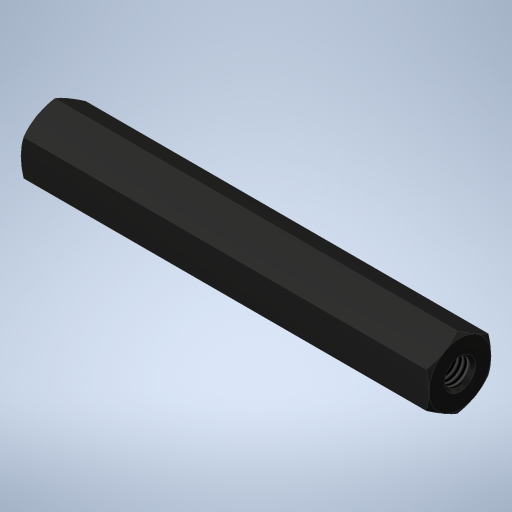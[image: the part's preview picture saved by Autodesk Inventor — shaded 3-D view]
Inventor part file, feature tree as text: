
AUTODESK INVENTOR PART (.ipt)
format: ipt  version: 2024.2 (Build 282272000, 272)  size: 286,720 bytes
history: native  units: mm
features: other x7, sketch x4, hole x2, revolve x1, extrude x1
ambient origin geometry x8: Origin, YZ Plane, XZ Plane, XY Plane, X Axis, Y Axis, Z Axis, Center Point
bodies: Solid1 (feature_tree)
feature tree (15):
  revolve  "Revolution1"  [1 undecoded]
  extrude  "Extrusion1"  TaperAngle=0.0deg  [1 undecoded]
  hole  "Hole1"  [1 undecoded]
  hole  "Hole2"  [1 undecoded]
  other  "C3_XY"
  other  "C3_YZ"
  other  "C3_ZX"
  other  "C3_X"
  other  "C3_Y"
  other  "C3_Z"
  other  "C3_Center"
  sketch  "Sketch_1"  dims[d0=360.0deg d1=39.5mm d2=0.0mm]
  sketch  "Sketch_2"  dims[d3=2.459mm d4=6.0mm d5=3.0mm d6=2.0mm d7=90.0deg d8=8.290148mm d9=120.0deg]
  sketch  "Sketch3"  dims[d10=2.459mm d11=6.0mm d12=3.0mm d13=2.0mm d14=90.0deg d15=8.290148mm d16=120.0deg d17=0.0mm]
  sketch  "Sketch4"
note: 4 required parameter values undecoded (feature->parameter linkage not recoverable at this tier; creation-order binding heuristic only, values carry confidence <= 0.55)